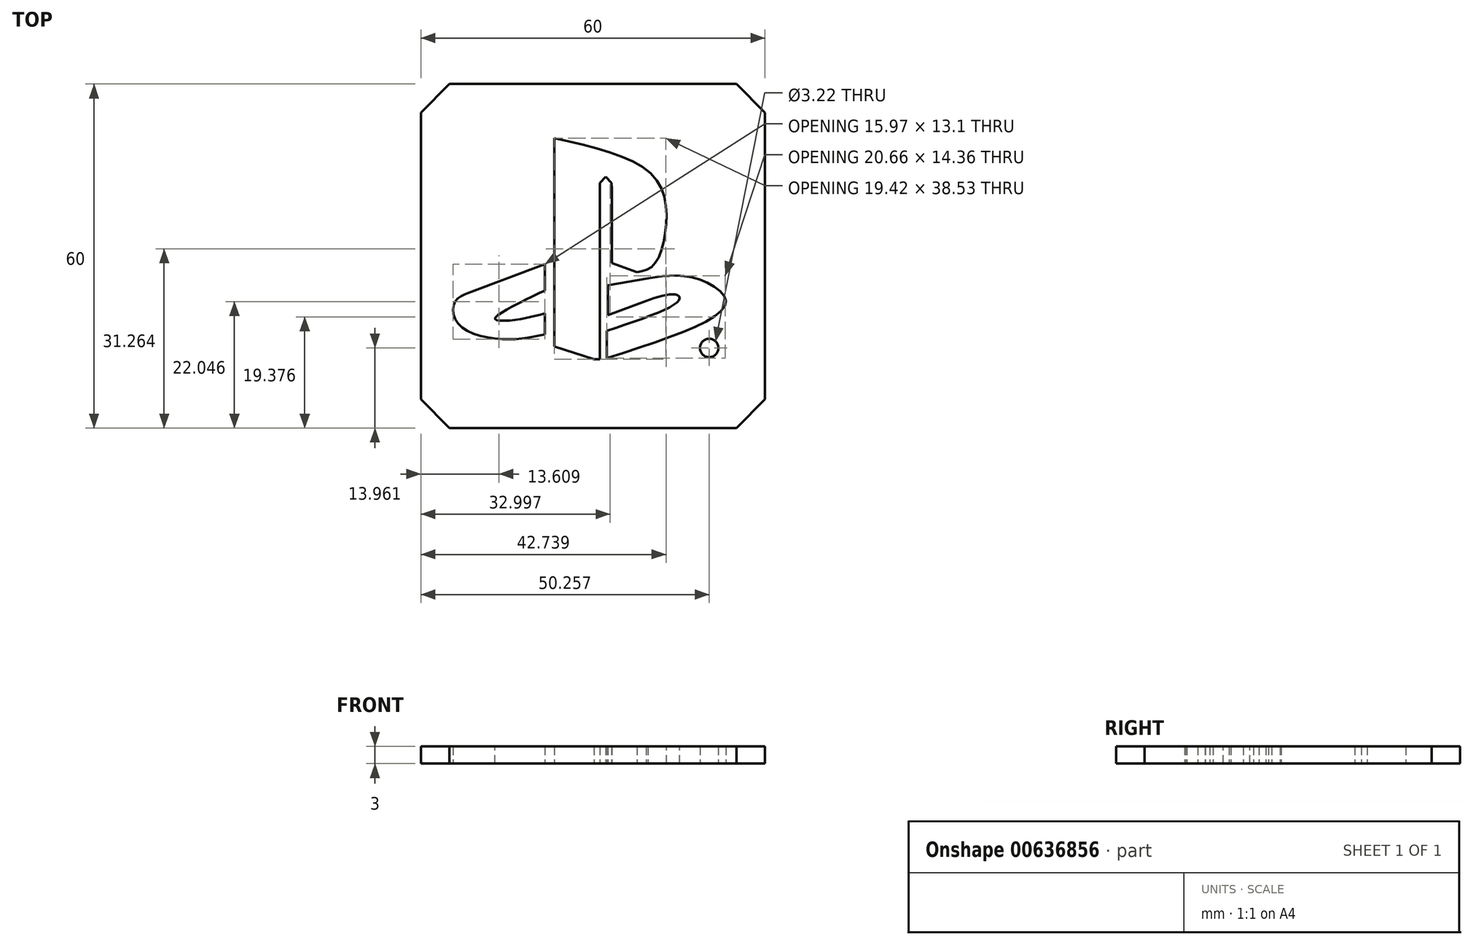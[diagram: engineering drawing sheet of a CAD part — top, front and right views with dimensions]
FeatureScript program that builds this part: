
annotation { "Feature Type Name" : "Feature", "Feature Type Description" : "" }
export const myFeature = defineFeature(function(context is Context, id is Id, definition is map)
    precondition{}
    {
        {
            var Q0;
            Q0=qCreatedBy(makeId("Top.planeOp"),FACE);
            var sketch = newSketch(context, id + "F0", { "sketchPlane" : qUnion([Q0])});
            skLineSegment(sketch, "E0", {"start": v(-5.03, 20.83) * mm, "end": v(-5.03, -39.17) * mm});
            skLineSegment(sketch, "E1", {"start": v(-5.03, -39.17) * mm, "end": v(54.97, -39.17) * mm});
            skLineSegment(sketch, "E2", {"start": v(54.97, -39.17) * mm, "end": v(54.97, 20.83) * mm});
            skLineSegment(sketch, "E3", {"start": v(54.97, 20.83) * mm, "end": v(-5.03, 20.83) * mm});
            skLineSegment(sketch, "E4", {"start": v(18.26, 11.36) * mm, "end": v(18.26, -24.92) * mm});
            skLineSegment(sketch, "E5", {"start": v(18.26, -24.92) * mm, "end": v(25.18, -27.17) * mm});
            skLineSegment(sketch, "E6", {"start": v(25.18, -27.17) * mm, "end": v(26.16, -27.17) * mm});
            skLineSegment(sketch, "E7", {"start": v(26.16, -27.17) * mm, "end": v(26.16, 1.76) * mm});
            skLineSegment(sketch, "E8", {"start": v(26.16, 1.76) * mm, "end": v(26.16, 3.6) * mm});
            skLineSegment(sketch, "E9", {"start": v(26.16, 3.6) * mm, "end": v(27.19, 4.62) * mm});
            skLineSegment(sketch, "E10", {"start": v(27.19, 4.62) * mm, "end": v(28.21, 3.6) * mm});
            skLineSegment(sketch, "E11", {"start": v(28.28, 2.47) * mm, "end": v(28.28, -10.38) * mm});
            skLineSegment(sketch, "E12", {"start": v(28.28, -10.38) * mm, "end": v(32.66, -12) * mm});
            skLineSegment(sketch, "E13", {"start": v(28.21, 3.6) * mm, "end": v(28.28, 2.47) * mm});
            skFitSpline(sketch, "E14", {"points": [v(32.66, -12) * mm, v(35.48, -10.8) * mm, v(37.67, -4.3) * mm, v(35.55, 4.73) * mm, v(18.26, 11.36) * mm], "startDerivative": vector(20.33, 3.96) * mm, "endDerivative": vector(-57.84, 12.92) * mm});
            skLineSegment(sketch, "E15", {"start": v(16.56, -10.58) * mm, "end": v(3.26, -15.6) * mm});
            skLineSegment(sketch, "E16", {"start": v(16.56, -10.58) * mm, "end": v(16.56, -15.2) * mm});
            skLineSegment(sketch, "E17", {"start": v(16.56, -19.16) * mm, "end": v(16.56, -22.82) * mm});
            skFitSpline(sketch, "E18", {"points": [v(16.56, -22.82) * mm, v(9.73, -23.67) * mm, v(1.53, -21.05) * mm, v(0.91, -17.15) * mm, v(3.26, -15.6) * mm], "startDerivative": vector(-22.05, -4.88) * mm, "endDerivative": vector(15.52, 5.78) * mm});
            skFitSpline(sketch, "E19", {"points": [v(16.56, -19.16) * mm, v(11.11, -20.35) * mm, v(7.9, -20.11) * mm, v(11.27, -17.79) * mm, v(16.56, -15.2) * mm], "startDerivative": vector(-19.05, -5.27) * mm, "endDerivative": vector(17.73, 8.34) * mm});
            skLineSegment(sketch, "E20", {"start": v(27.56, -14.26) * mm, "end": v(34.53, -13.05) * mm});
            skFitSpline(sketch, "E21", {"points": [v(34.53, -13.05) * mm, v(42.79, -13.05) * mm, v(48.14, -17.23) * mm, v(27.38, -26.97) * mm], "startDerivative": vector(28.65, 4.3) * mm, "endDerivative": vector(-66, -21.04) * mm});
            skLineSegment(sketch, "E22", {"start": v(27.38, -26.97) * mm, "end": v(27.38, -22.23) * mm});
            skLineSegment(sketch, "E23", {"start": v(27.56, -14.26) * mm, "end": v(27.56, -19.45) * mm});
            skLineSegment(sketch, "E24", {"start": v(27.56, -19.45) * mm, "end": v(34.25, -16.98) * mm});
            skFitSpline(sketch, "E25", {"points": [v(34.25, -16.98) * mm, v(38.2, -15.88) * mm, v(39.9, -16.1) * mm, v(39.88, -16.98) * mm, v(27.38, -22.23) * mm], "startDerivative": vector(16.43, 5.65) * mm, "endDerivative": vector(-37.07, -12.48) * mm});
            skCircle(sketch, "E26", {"center": v(45.23, -25.2) * mm, "radius": 1.61 * mm});
            skLineSegment(sketch, "E27", {"start": v(44.53, -24.36) * mm, "end": v(44.53, -26.22) * mm});
            skLineSegment(sketch, "E28", {"start": v(44.53, -24.36) * mm, "end": v(45.67, -24.36) * mm});
            skLineSegment(sketch, "E29", {"start": v(45.67, -24.36) * mm, "end": v(45.98, -25.2) * mm});
            skLineSegment(sketch, "E30", {"start": v(45.98, -25.2) * mm, "end": v(45.67, -25.32) * mm});
            skLineSegment(sketch, "E31", {"start": v(45.67, -25.32) * mm, "end": v(45.98, -26.17) * mm});
            skLineSegment(sketch, "E32", {"start": v(45.98, -26.17) * mm, "end": v(45.67, -26.28) * mm});
            skLineSegment(sketch, "E33", {"start": v(45.67, -26.28) * mm, "end": v(45.23, -25.71) * mm});
            skLineSegment(sketch, "E34", {"start": v(45.23, -25.71) * mm, "end": v(44.91, -25.83) * mm});
            skLineSegment(sketch, "E35", {"start": v(44.91, -25.83) * mm, "end": v(44.53, -26.22) * mm});
            skSolve(sketch);
        }
        {
            var Q0;
            Q0=makeQuery(id+"F0.imprint","IMPRINT",FACE,{"disambiguationData":[TD([[makeQuery(id+"F0.imprint","IMPRINT",EDGE,{"derivedFrom":sQuery(id+"F0.wireOp",EDGE,"E0")}),1.0]])]});
            extrude(context, id + "F1", {"entities" : qUnion([Q0]), "depth" : 3 * mm, "offsetDistance" : 25 * mm});
        }
        {
            var Q0;
            Q0=makeQuery(id+"F1.opExtrude","SWEPT_EDGE",EDGE,{"disambiguationData":[OSD([sQuery(id+"F0.wireOp",EDGE,"E0"),sQuery(id+"F0.wireOp",EDGE,"E3")])]});
            var Q1;
            Q1=makeQuery(id+"F1.opExtrude","SWEPT_EDGE",EDGE,{"disambiguationData":[OSD([sQuery(id+"F0.wireOp",EDGE,"E0"),sQuery(id+"F0.wireOp",EDGE,"E1")])]});
            var Q2;
            Q2=makeQuery(id+"F1.opExtrude","SWEPT_EDGE",EDGE,{"disambiguationData":[OSD([sQuery(id+"F0.wireOp",EDGE,"E1"),sQuery(id+"F0.wireOp",EDGE,"E2")])]});
            var Q3;
            Q3=makeQuery(id+"F1.opExtrude","SWEPT_EDGE",EDGE,{"disambiguationData":[OSD([sQuery(id+"F0.wireOp",EDGE,"E2"),sQuery(id+"F0.wireOp",EDGE,"E3")])]});
            chamfer(context, id + "F2", {"entities" : qUnion([Q0, Q1, Q2, Q3]), "width" : 5 * mm, "tangentPropagation" : true});
        }
    });
